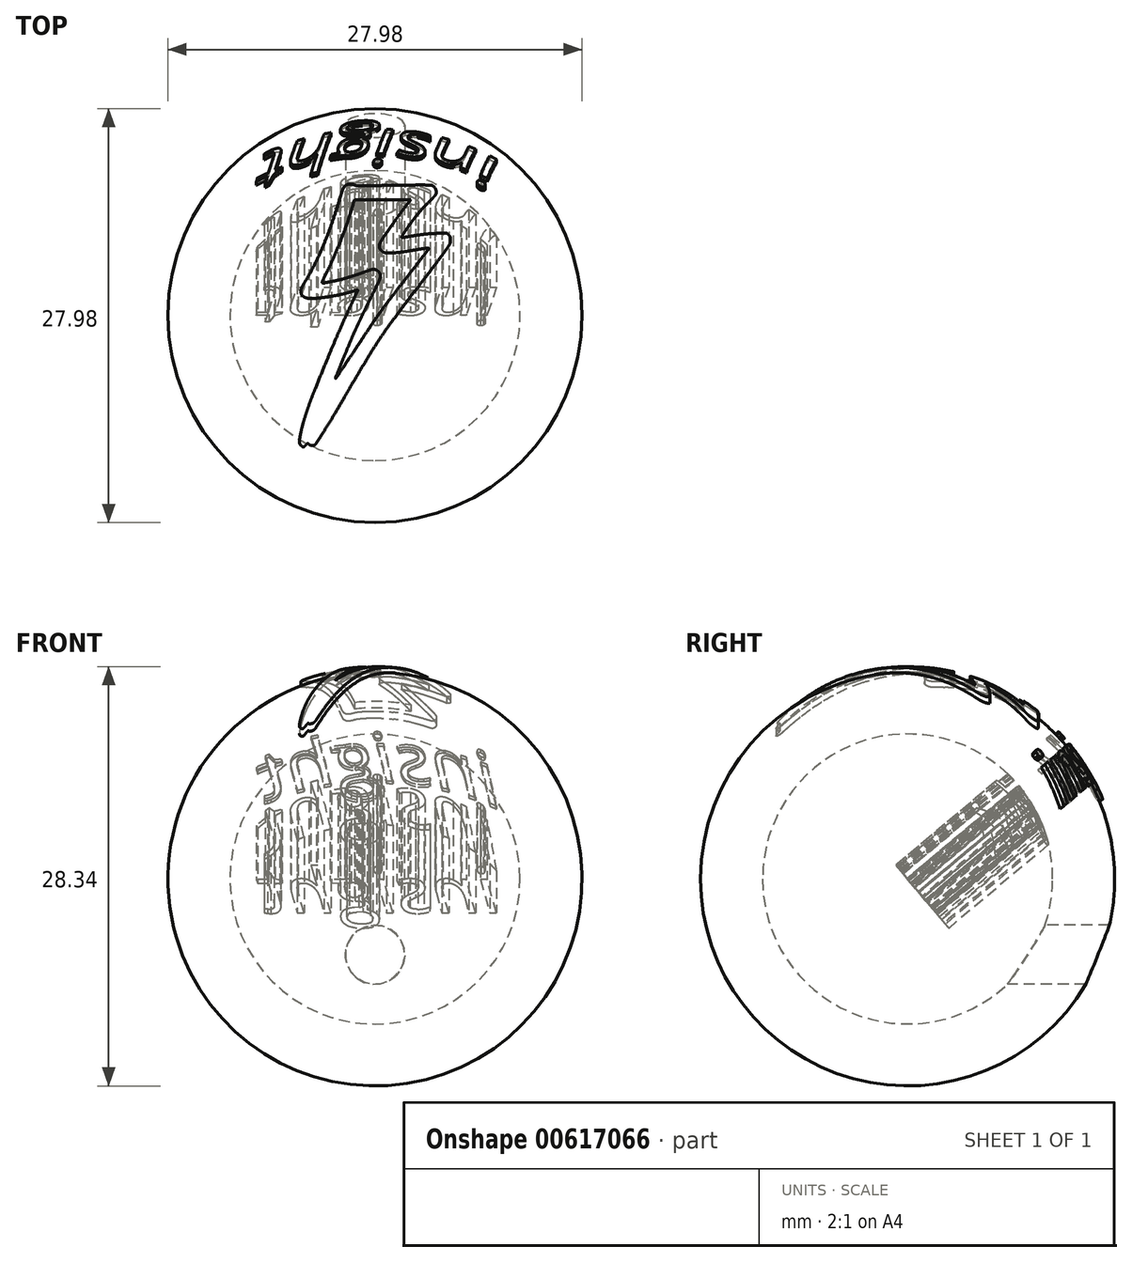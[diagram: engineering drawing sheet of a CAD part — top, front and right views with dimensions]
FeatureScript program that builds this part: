
annotation { "Feature Type Name" : "Feature", "Feature Type Description" : "" }
export const myFeature = defineFeature(function(context is Context, id is Id, definition is map)
    precondition{}
    {
        {
            var Q0;
            Q0=qCreatedBy(makeId("Top.planeOp"),FACE);
            var sketch = newSketch(context, id + "F0", { "sketchPlane" : qUnion([Q0])});
            skLineSegment(sketch, "E0", {"start": v(0, -10) * mm, "end": v(0, 10) * mm});
            skArc(sketch, "E1", {"start": v(0, 10) * mm, "mid": v(-10, 0) * mm, "end": v(0, -10) * mm});
            skSolve(sketch);
        }
        {
            var Q0;
            {var subQ0=sQuery(id+"F0.wireOp",EDGE,"E1");Q0=makeQuery(id+"F0.imprint","IMPRINT",FACE,{"disambiguationData":[TD([[makeQuery(id+"F0.imprint","IMPRINT",EDGE,{"derivedFrom":subQ0}),1.0]])]});}
            var Q1;
            Q1=sQuery(id+"F0.wireOp",EDGE,"E0");
            revolve(context, id + "F1", {"entities" : qUnion([Q0]), "axis" : qUnion([Q1]), "revolveType" : RevolveType.FULL});
        }
        {
            var Q0;
            Q0=makeQuery(id+"F1.opRevolve","SWEPT_BODY",BODY,{"disambiguationData":[OSD([sQuery(id+"F0.wireOp",EDGE,"E0"),sQuery(id+"F0.wireOp",EDGE,"E1")])]});
            var Q1;
            Q1=sQuery(id+"F0.wireOp",VERTEX,"NPe4G0ez-t7S9-9isL-QO5v-uuJu600mHcIT.center");
            var Q2;
            Q2=sQuery(id+"F0.wireOp",VERTEX,"E1.center");
            transform(context, id + "F2", {"entities" : qUnion([Q0]), "transformType" : TransformType.SCALE_UNIFORMLY, "scale" : 33.3, "scalePoint" : qUnion([Q2]), "makeCopy" : false});
        }
        {
            var Q0;
            Q0=qCreatedBy(makeId("Top.planeOp"),FACE);
            var sketch = newSketch(context, id + "F3", { "sketchPlane" : qUnion([Q0])});
            skArc(sketch, "E2", {"start": v(-47, 209.54) * mm, "mid": v(-48.28, 208.6) * mm, "end": v(-49.38, 207.48) * mm});
            skArc(sketch, "E3", {"start": v(-49.38, 207.48) * mm, "mid": v(-50.34, 206.13) * mm, "end": v(-51.1, 204.66) * mm});
            skArc(sketch, "E4", {"start": v(-51.1, 204.66) * mm, "mid": v(-52.12, 202.08) * mm, "end": v(-53.02, 199.45) * mm});
            skArc(sketch, "E5", {"start": v(-53.02, 199.45) * mm, "mid": v(-55.26, 192.2) * mm, "end": v(-57.48, 184.96) * mm});
            skArc(sketch, "E6", {"start": v(-57.48, 184.96) * mm, "mid": v(-63.5, 165.86) * mm, "end": v(-69.92, 146.9) * mm});
            skArc(sketch, "E7", {"start": v(-69.92, 146.9) * mm, "mid": v(-76.05, 130.2) * mm, "end": v(-82.66, 113.68) * mm});
            skArc(sketch, "E8", {"start": v(-82.66, 113.68) * mm, "mid": v(-89.16, 98.83) * mm, "end": v(-96.13, 84.2) * mm});
            skArc(sketch, "E9", {"start": v(-96.13, 84.2) * mm, "mid": v(-103.18, 70.68) * mm, "end": v(-110.76, 57.45) * mm});
            skArc(sketch, "E10", {"start": v(-110.76, 57.45) * mm, "mid": v(-113.7, 52.45) * mm, "end": v(-116.55, 47.39) * mm});
            skArc(sketch, "E11", {"start": v(-116.55, 47.39) * mm, "mid": v(-117.87, 44.67) * mm, "end": v(-118.89, 41.82) * mm});
            skArc(sketch, "E12", {"start": v(-118.89, 41.82) * mm, "mid": v(-119.28, 39.76) * mm, "end": v(-119.24, 37.66) * mm});
            skArc(sketch, "E13", {"start": v(-119.24, 37.66) * mm, "mid": v(-118.78, 35.5) * mm, "end": v(-117.95, 33.47) * mm});
            skArc(sketch, "E14", {"start": v(-117.95, 33.47) * mm, "mid": v(-117.53, 32.77) * mm, "end": v(-117.02, 32.12) * mm});
            skArc(sketch, "E15", {"start": v(-117.02, 32.12) * mm, "mid": v(-116.39, 31.48) * mm, "end": v(-115.7, 30.9) * mm});
            skArc(sketch, "E16", {"start": v(-115.7, 30.9) * mm, "mid": v(-114.87, 30.32) * mm, "end": v(-114, 29.8) * mm});
            skArc(sketch, "E17", {"start": v(-114, 29.8) * mm, "mid": v(-113, 29.32) * mm, "end": v(-111.97, 28.89) * mm});
            skArc(sketch, "E18", {"start": v(-111.97, 28.89) * mm, "mid": v(-106.69, 27.5) * mm, "end": v(-101.23, 27.25) * mm});
            skArc(sketch, "E19", {"start": v(-101.23, 27.25) * mm, "mid": v(-90.7, 28.1) * mm, "end": v(-80.2, 29.33) * mm});
            skArc(sketch, "E20", {"start": v(-80.2, 29.33) * mm, "mid": v(-68.36, 31.17) * mm, "end": v(-56.6, 33.47) * mm});
            skArc(sketch, "E21", {"start": v(-56.6, 33.47) * mm, "mid": v(-45.47, 36.14) * mm, "end": v(-34.47, 39.32) * mm});
            skArc(sketch, "E22", {"start": v(-34.47, 39.32) * mm, "mid": v(-33.22, 39.7) * mm, "end": v(-31.97, 40.07) * mm});
            skArc(sketch, "E23", {"start": v(-31.97, 40.07) * mm, "mid": v(-30.9, 40.37) * mm, "end": v(-29.82, 40.66) * mm});
            skArc(sketch, "E24", {"start": v(-29.82, 40.66) * mm, "mid": v(-28.9, 40.88) * mm, "end": v(-27.98, 41.1) * mm});
            skArc(sketch, "E25", {"start": v(-27.98, 41.1) * mm, "mid": v(-27.83, 41.1) * mm, "end": v(-27.7, 41.03) * mm});
            skArc(sketch, "E26", {"start": v(-27.7, 41.03) * mm, "mid": v(-27.63, 40.9) * mm, "end": v(-27.65, 40.74) * mm});
            skArc(sketch, "E27", {"start": v(-27.65, 40.74) * mm, "mid": v(-29.01, 37.7) * mm, "end": v(-30.38, 34.67) * mm});
            skArc(sketch, "E28", {"start": v(-30.38, 34.67) * mm, "mid": v(-31.94, 31.26) * mm, "end": v(-33.51, 27.85) * mm});
            skArc(sketch, "E29", {"start": v(-33.51, 27.85) * mm, "mid": v(-35.4, 23.83) * mm, "end": v(-37.29, 19.82) * mm});
            skArc(sketch, "E30", {"start": v(-37.29, 19.82) * mm, "mid": v(-43.49, 6.55) * mm, "end": v(-49.54, -6.8) * mm});
            skArc(sketch, "E31", {"start": v(-49.54, -6.8) * mm, "mid": v(-56.04, -21.49) * mm, "end": v(-62.42, -36.24) * mm});
            skArc(sketch, "E32", {"start": v(-62.42, -36.24) * mm, "mid": v(-70.03, -54.2) * mm, "end": v(-77.53, -72.22) * mm});
            skArc(sketch, "E33", {"start": v(-77.53, -72.22) * mm, "mid": v(-87.24, -95.89) * mm, "end": v(-96.88, -119.58) * mm});
            skArc(sketch, "E34", {"start": v(-96.88, -119.58) * mm, "mid": v(-100.55, -128.83) * mm, "end": v(-104.07, -138.15) * mm});
            skArc(sketch, "E35", {"start": v(-104.07, -138.15) * mm, "mid": v(-107.3, -147.19) * mm, "end": v(-110.39, -156.28) * mm});
            skArc(sketch, "E36", {"start": v(-110.39, -156.28) * mm, "mid": v(-113, -164.53) * mm, "end": v(-115.47, -172.82) * mm});
            skArc(sketch, "E37", {"start": v(-115.47, -172.82) * mm, "mid": v(-117.29, -179.6) * mm, "end": v(-118.86, -186.44) * mm});
            skArc(sketch, "E38", {"start": v(-118.86, -186.44) * mm, "mid": v(-119.99, -191.95) * mm, "end": v(-121.04, -197.48) * mm});
            skArc(sketch, "E39", {"start": v(-121.04, -197.48) * mm, "mid": v(-121.43, -200.27) * mm, "end": v(-121.57, -203.08) * mm});
            skArc(sketch, "E40", {"start": v(-121.57, -203.08) * mm, "mid": v(-121.42, -204.86) * mm, "end": v(-120.93, -206.57) * mm});
            skArc(sketch, "E41", {"start": v(-120.93, -206.57) * mm, "mid": v(-120.15, -208.02) * mm, "end": v(-119.04, -209.23) * mm});
            skArc(sketch, "E42", {"start": v(-119.04, -209.23) * mm, "mid": v(-117.89, -210.16) * mm, "end": v(-116.67, -211) * mm});
            skArc(sketch, "E43", {"start": v(-116.67, -211) * mm, "mid": v(-115.93, -211.32) * mm, "end": v(-115.12, -211.37) * mm});
            skArc(sketch, "E44", {"start": v(-115.12, -211.37) * mm, "mid": v(-114.28, -211.14) * mm, "end": v(-113.53, -210.67) * mm});
            skArc(sketch, "E45", {"start": v(-113.53, -210.67) * mm, "mid": v(-112.18, -209.48) * mm, "end": v(-110.88, -208.23) * mm});
            skArc(sketch, "E46", {"start": v(-110.88, -208.23) * mm, "mid": v(-110.09, -207.46) * mm, "end": v(-109.28, -206.72) * mm});
            skArc(sketch, "E47", {"start": v(-109.28, -206.72) * mm, "mid": v(-108.75, -206.3) * mm, "end": v(-108.19, -205.97) * mm});
            skArc(sketch, "E48", {"start": v(-108.19, -205.97) * mm, "mid": v(-107.84, -205.86) * mm, "end": v(-107.47, -205.86) * mm});
            skArc(sketch, "E49", {"start": v(-107.47, -205.86) * mm, "mid": v(-107.19, -205.98) * mm, "end": v(-107, -206.23) * mm});
            skArc(sketch, "E50", {"start": v(-107, -206.23) * mm, "mid": v(-106.57, -207.01) * mm, "end": v(-105.92, -207.63) * mm});
            skArc(sketch, "E51", {"start": v(-105.92, -207.63) * mm, "mid": v(-104.9, -208.26) * mm, "end": v(-103.81, -208.75) * mm});
            skArc(sketch, "E52", {"start": v(-103.81, -208.75) * mm, "mid": v(-102.6, -209.13) * mm, "end": v(-101.34, -209.36) * mm});
            skArc(sketch, "E53", {"start": v(-101.34, -209.36) * mm, "mid": v(-100.23, -209.39) * mm, "end": v(-99.13, -209.22) * mm});
            skArc(sketch, "E54", {"start": v(-99.13, -209.22) * mm, "mid": v(-96.8, -208.14) * mm, "end": v(-95, -206.3) * mm});
            skArc(sketch, "E55", {"start": v(-95, -206.3) * mm, "mid": v(-88.97, -197.13) * mm, "end": v(-83.04, -187.9) * mm});
            skArc(sketch, "E56", {"start": v(-83.04, -187.9) * mm, "mid": v(-74.78, -174.65) * mm, "end": v(-66.71, -161.28) * mm});
            skArc(sketch, "E57", {"start": v(-66.71, -161.28) * mm, "mid": v(-54.28, -140.2) * mm, "end": v(-41.93, -119.08) * mm});
            skArc(sketch, "E58", {"start": v(-41.93, -119.08) * mm, "mid": v(-27, -93.64) * mm, "end": v(-11.87, -68.32) * mm});
            skArc(sketch, "E59", {"start": v(-11.87, -68.32) * mm, "mid": v(-1.4, -51.44) * mm, "end": v(9.47, -34.82) * mm});
            skArc(sketch, "E60", {"start": v(9.47, -34.82) * mm, "mid": v(20.75, -18.5) * mm, "end": v(32.43, -2.45) * mm});
            skArc(sketch, "E61", {"start": v(32.43, -2.45) * mm, "mid": v(50.15, 21.06) * mm, "end": v(68.05, 44.42) * mm});
            skArc(sketch, "E62", {"start": v(68.05, 44.42) * mm, "mid": v(76.36, 55.22) * mm, "end": v(84.65, 66.03) * mm});
            skArc(sketch, "E63", {"start": v(84.65, 66.03) * mm, "mid": v(91.6, 75.18) * mm, "end": v(98.52, 84.35) * mm});
            skArc(sketch, "E64", {"start": v(98.52, 84.35) * mm, "mid": v(104, 91.7) * mm, "end": v(109.45, 99.07) * mm});
            skArc(sketch, "E65", {"start": v(109.45, 99.07) * mm, "mid": v(112.83, 103.75) * mm, "end": v(116.12, 108.5) * mm});
            skArc(sketch, "E66", {"start": v(116.12, 108.5) * mm, "mid": v(117.67, 110.82) * mm, "end": v(119.18, 113.17) * mm});
            skArc(sketch, "E67", {"start": v(119.18, 113.17) * mm, "mid": v(119.98, 114.55) * mm, "end": v(120.65, 116) * mm});
            skArc(sketch, "E68", {"start": v(120.65, 116) * mm, "mid": v(121.08, 117.22) * mm, "end": v(121.35, 118.48) * mm});
            skArc(sketch, "E69", {"start": v(121.35, 118.48) * mm, "mid": v(121.51, 120) * mm, "end": v(121.57, 121.54) * mm});
            skArc(sketch, "E70", {"start": v(121.57, 121.54) * mm, "mid": v(121.54, 122.95) * mm, "end": v(121.45, 124.35) * mm});
            skArc(sketch, "E71", {"start": v(121.45, 124.35) * mm, "mid": v(121.3, 125.3) * mm, "end": v(121.02, 126.22) * mm});
            skArc(sketch, "E72", {"start": v(121.02, 126.22) * mm, "mid": v(120.64, 127.04) * mm, "end": v(120.14, 127.8) * mm});
            skArc(sketch, "E73", {"start": v(120.14, 127.8) * mm, "mid": v(119.36, 128.74) * mm, "end": v(118.52, 129.63) * mm});
            skLineSegment(sketch, "E74", {"start": v(118.52, 129.63) * mm, "end": v(115.47, 132.68) * mm});
            skLineSegment(sketch, "E75", {"start": v(115.47, 132.68) * mm, "end": v(98.77, 132.14) * mm});
            skArc(sketch, "E76", {"start": v(98.77, 132.14) * mm, "mid": v(94.4, 131.97) * mm, "end": v(90.03, 131.72) * mm});
            skArc(sketch, "E77", {"start": v(90.03, 131.72) * mm, "mid": v(85.84, 131.4) * mm, "end": v(81.65, 131.01) * mm});
            skArc(sketch, "E78", {"start": v(81.65, 131.01) * mm, "mid": v(77.34, 130.53) * mm, "end": v(73.04, 129.97) * mm});
            skArc(sketch, "E79", {"start": v(73.04, 129.97) * mm, "mid": v(68.3, 129.28) * mm, "end": v(63.57, 128.52) * mm});
            skArc(sketch, "E80", {"start": v(63.57, 128.52) * mm, "mid": v(59.96, 127.92) * mm, "end": v(56.35, 127.34) * mm});
            skArc(sketch, "E81", {"start": v(56.35, 127.34) * mm, "mid": v(53.16, 126.83) * mm, "end": v(49.97, 126.34) * mm});
            skArc(sketch, "E82", {"start": v(49.97, 126.34) * mm, "mid": v(47.26, 125.93) * mm, "end": v(44.55, 125.53) * mm});
            skArc(sketch, "E83", {"start": v(44.55, 125.53) * mm, "mid": v(43.9, 125.45) * mm, "end": v(43.25, 125.43) * mm});
            skArc(sketch, "E84", {"start": v(43.25, 125.43) * mm, "mid": v(42.86, 125.61) * mm, "end": v(42.77, 126.03) * mm});
            skArc(sketch, "E85", {"start": v(42.77, 126.03) * mm, "mid": v(43.04, 126.93) * mm, "end": v(43.43, 127.78) * mm});
            skArc(sketch, "E86", {"start": v(43.43, 127.78) * mm, "mid": v(44.33, 129.4) * mm, "end": v(45.32, 130.97) * mm});
            skArc(sketch, "E87", {"start": v(45.32, 130.97) * mm, "mid": v(47.23, 133.83) * mm, "end": v(49.18, 136.67) * mm});
            skArc(sketch, "E88", {"start": v(49.18, 136.67) * mm, "mid": v(54.18, 143.84) * mm, "end": v(59.27, 150.95) * mm});
            skArc(sketch, "E89", {"start": v(59.27, 150.95) * mm, "mid": v(63.33, 156.4) * mm, "end": v(67.53, 161.75) * mm});
            skArc(sketch, "E90", {"start": v(67.53, 161.75) * mm, "mid": v(71.4, 166.4) * mm, "end": v(75.39, 170.92) * mm});
            skArc(sketch, "E91", {"start": v(75.39, 170.92) * mm, "mid": v(79.69, 175.52) * mm, "end": v(84.11, 180.02) * mm});
            skArc(sketch, "E92", {"start": v(84.11, 180.02) * mm, "mid": v(86.5, 182.4) * mm, "end": v(88.88, 184.8) * mm});
            skArc(sketch, "E93", {"start": v(88.88, 184.8) * mm, "mid": v(90.99, 186.98) * mm, "end": v(93.07, 189.17) * mm});
            skArc(sketch, "E94", {"start": v(93.07, 189.17) * mm, "mid": v(94.8, 191.03) * mm, "end": v(96.53, 192.9) * mm});
            skArc(sketch, "E95", {"start": v(96.53, 192.9) * mm, "mid": v(97.03, 193.52) * mm, "end": v(97.45, 194.2) * mm});
            skArc(sketch, "E96", {"start": v(97.45, 194.2) * mm, "mid": v(98.2, 196.08) * mm, "end": v(98.5, 198.08) * mm});
            skArc(sketch, "E97", {"start": v(98.5, 198.08) * mm, "mid": v(98.4, 200.27) * mm, "end": v(97.9, 202.4) * mm});
            skArc(sketch, "E98", {"start": v(97.9, 202.4) * mm, "mid": v(97.03, 204.43) * mm, "end": v(95.8, 206.27) * mm});
            skArc(sketch, "E99", {"start": v(95.8, 206.27) * mm, "mid": v(94.34, 207.76) * mm, "end": v(92.6, 208.9) * mm});
            skArc(sketch, "E100", {"start": v(92.6, 208.9) * mm, "mid": v(91.01, 209.52) * mm, "end": v(89.33, 209.78) * mm});
            skArc(sketch, "E101", {"start": v(89.33, 209.78) * mm, "mid": v(84.65, 209.93) * mm, "end": v(79.96, 210.01) * mm});
            skArc(sketch, "E102", {"start": v(79.96, 210.01) * mm, "mid": v(72.03, 210.05) * mm, "end": v(64.1, 209.99) * mm});
            skArc(sketch, "E103", {"start": v(64.1, 209.99) * mm, "mid": v(46.76, 209.76) * mm, "end": v(29.42, 209.5) * mm});
            skArc(sketch, "E104", {"start": v(29.42, 209.5) * mm, "mid": v(12.64, 209.26) * mm, "end": v(-4.14, 209.04) * mm});
            skArc(sketch, "E105", {"start": v(-4.14, 209.04) * mm, "mid": v(-12.26, 208.98) * mm, "end": v(-20.37, 209) * mm});
            skArc(sketch, "E106", {"start": v(-20.37, 209) * mm, "mid": v(-25.38, 209.07) * mm, "end": v(-30.39, 209.19) * mm});
            skArc(sketch, "E107", {"start": v(-30.39, 209.19) * mm, "mid": v(-31.67, 209.42) * mm, "end": v(-32.84, 210) * mm});
            skArc(sketch, "E108", {"start": v(-32.84, 210) * mm, "mid": v(-34.16, 210.72) * mm, "end": v(-35.6, 211.12) * mm});
            skArc(sketch, "E109", {"start": v(-35.6, 211.12) * mm, "mid": v(-37.61, 211.34) * mm, "end": v(-39.63, 211.37) * mm});
            skArc(sketch, "E110", {"start": v(-39.63, 211.37) * mm, "mid": v(-41.72, 211.2) * mm, "end": v(-43.79, 210.84) * mm});
            skArc(sketch, "E111", {"start": v(-43.79, 210.84) * mm, "mid": v(-45.45, 210.32) * mm, "end": v(-47, 209.54) * mm});
            skArc(sketch, "E112", {"start": v(55.04, 183.12) * mm, "mid": v(51.95, 179.25) * mm, "end": v(48.92, 175.34) * mm});
            skArc(sketch, "E113", {"start": v(48.92, 175.34) * mm, "mid": v(45.58, 170.93) * mm, "end": v(42.28, 166.49) * mm});
            skArc(sketch, "E114", {"start": v(42.28, 166.49) * mm, "mid": v(38.29, 161) * mm, "end": v(34.33, 155.49) * mm});
            skArc(sketch, "E115", {"start": v(34.33, 155.49) * mm, "mid": v(29.19, 148.22) * mm, "end": v(24.07, 140.94) * mm});
            skArc(sketch, "E116", {"start": v(24.07, 140.94) * mm, "mid": v(17.9, 132.06) * mm, "end": v(11.83, 123.12) * mm});
            skArc(sketch, "E117", {"start": v(11.83, 123.12) * mm, "mid": v(9.53, 119.34) * mm, "end": v(7.6, 115.36) * mm});
            skArc(sketch, "E118", {"start": v(7.6, 115.36) * mm, "mid": v(6.92, 112.88) * mm, "end": v(6.94, 110.3) * mm});
            skArc(sketch, "E119", {"start": v(6.94, 110.3) * mm, "mid": v(7.64, 107.86) * mm, "end": v(9, 105.7) * mm});
            skArc(sketch, "E120", {"start": v(9, 105.7) * mm, "mid": v(9.6, 105.02) * mm, "end": v(10.27, 104.4) * mm});
            skArc(sketch, "E121", {"start": v(10.27, 104.4) * mm, "mid": v(11.09, 103.74) * mm, "end": v(11.94, 103.12) * mm});
            skArc(sketch, "E122", {"start": v(11.94, 103.12) * mm, "mid": v(12.8, 102.56) * mm, "end": v(13.7, 102.04) * mm});
            skArc(sketch, "E123", {"start": v(13.7, 102.04) * mm, "mid": v(14.49, 101.66) * mm, "end": v(15.3, 101.35) * mm});
            skArc(sketch, "E124", {"start": v(15.3, 101.35) * mm, "mid": v(18.1, 100.67) * mm, "end": v(20.97, 100.47) * mm});
            skArc(sketch, "E125", {"start": v(20.97, 100.47) * mm, "mid": v(26.03, 100.6) * mm, "end": v(31.08, 100.9) * mm});
            skArc(sketch, "E126", {"start": v(31.08, 100.9) * mm, "mid": v(37.67, 101.52) * mm, "end": v(44.24, 102.34) * mm});
            skArc(sketch, "E127", {"start": v(44.24, 102.34) * mm, "mid": v(52.42, 103.55) * mm, "end": v(60.57, 104.88) * mm});
            skArc(sketch, "E128", {"start": v(60.57, 104.88) * mm, "mid": v(67.14, 106) * mm, "end": v(73.7, 107.07) * mm});
            skArc(sketch, "E129", {"start": v(73.7, 107.07) * mm, "mid": v(77.4, 107.63) * mm, "end": v(81.12, 108.1) * mm});
            skArc(sketch, "E130", {"start": v(81.12, 108.1) * mm, "mid": v(83.48, 108.33) * mm, "end": v(85.85, 108.52) * mm});
            skArc(sketch, "E131", {"start": v(85.85, 108.52) * mm, "mid": v(86.36, 108.33) * mm, "end": v(86.57, 107.84) * mm});
            skArc(sketch, "E132", {"start": v(86.57, 107.84) * mm, "mid": v(86.49, 107.34) * mm, "end": v(86.25, 106.9) * mm});
            skArc(sketch, "E133", {"start": v(86.25, 106.9) * mm, "mid": v(81.5, 100.69) * mm, "end": v(76.75, 94.48) * mm});
            skArc(sketch, "E134", {"start": v(76.75, 94.48) * mm, "mid": v(70.88, 86.84) * mm, "end": v(64.97, 79.23) * mm});
            skArc(sketch, "E135", {"start": v(64.97, 79.23) * mm, "mid": v(56.84, 68.82) * mm, "end": v(48.7, 58.42) * mm});
            skArc(sketch, "E136", {"start": v(48.7, 58.42) * mm, "mid": v(39.42, 46.53) * mm, "end": v(30.2, 34.58) * mm});
            skArc(sketch, "E137", {"start": v(30.2, 34.58) * mm, "mid": v(22.75, 24.8) * mm, "end": v(15.4, 14.95) * mm});
            skArc(sketch, "E138", {"start": v(15.4, 14.95) * mm, "mid": v(9.27, 6.56) * mm, "end": v(3.24, -1.9) * mm});
            skArc(sketch, "E139", {"start": v(3.24, -1.9) * mm, "mid": v(-2, -9.44) * mm, "end": v(-7.1, -17.08) * mm});
            skArc(sketch, "E140", {"start": v(-7.1, -17.08) * mm, "mid": v(-18.13, -33.82) * mm, "end": v(-29.19, -50.55) * mm});
            skArc(sketch, "E141", {"start": v(-29.19, -50.55) * mm, "mid": v(-38.12, -64.02) * mm, "end": v(-47.09, -77.46) * mm});
            skArc(sketch, "E142", {"start": v(-47.09, -77.46) * mm, "mid": v(-54.97, -89.25) * mm, "end": v(-62.85, -101.03) * mm});
            skArc(sketch, "E143", {"start": v(-62.85, -101.03) * mm, "mid": v(-63.05, -101.15) * mm, "end": v(-63.26, -101.07) * mm});
            skArc(sketch, "E144", {"start": v(-63.26, -101.07) * mm, "mid": v(-63.52, -100.6) * mm, "end": v(-63.47, -100.08) * mm});
            skArc(sketch, "E145", {"start": v(-63.47, -100.08) * mm, "mid": v(-57.76, -85.98) * mm, "end": v(-52.06, -71.89) * mm});
            skArc(sketch, "E146", {"start": v(-52.06, -71.89) * mm, "mid": v(-46.78, -58.95) * mm, "end": v(-41.44, -46.04) * mm});
            skArc(sketch, "E147", {"start": v(-41.44, -46.04) * mm, "mid": v(-37.33, -36.33) * mm, "end": v(-33.11, -26.67) * mm});
            skArc(sketch, "E148", {"start": v(-33.11, -26.67) * mm, "mid": v(-30.81, -21.55) * mm, "end": v(-28.46, -16.44) * mm});
            skArc(sketch, "E149", {"start": v(-28.46, -16.44) * mm, "mid": v(-25.1, -9.3) * mm, "end": v(-21.72, -2.17) * mm});
            skArc(sketch, "E150", {"start": v(-21.72, -2.17) * mm, "mid": v(-18, 5.59) * mm, "end": v(-14.25, 13.33) * mm});
            skArc(sketch, "E151", {"start": v(-14.25, 13.33) * mm, "mid": v(-10.7, 20.58) * mm, "end": v(-7.13, 27.81) * mm});
            skArc(sketch, "E152", {"start": v(-7.13, 27.81) * mm, "mid": v(-0.89, 40.43) * mm, "end": v(5.29, 53.08) * mm});
            skArc(sketch, "E153", {"start": v(5.29, 53.08) * mm, "mid": v(7.1, 57.26) * mm, "end": v(8.5, 61.59) * mm});
            skArc(sketch, "E154", {"start": v(8.5, 61.59) * mm, "mid": v(8.8, 64.16) * mm, "end": v(8.26, 66.7) * mm});
            skArc(sketch, "E155", {"start": v(8.26, 66.7) * mm, "mid": v(6.91, 69.22) * mm, "end": v(5, 71.35) * mm});
            skArc(sketch, "E156", {"start": v(5, 71.35) * mm, "mid": v(3.35, 72.6) * mm, "end": v(1.52, 73.58) * mm});
            skArc(sketch, "E157", {"start": v(1.52, 73.58) * mm, "mid": v(-0.24, 74.14) * mm, "end": v(-2.07, 74.3) * mm});
            skArc(sketch, "E158", {"start": v(-2.07, 74.3) * mm, "mid": v(-4.42, 74.1) * mm, "end": v(-6.73, 73.58) * mm});
            skArc(sketch, "E159", {"start": v(-6.73, 73.58) * mm, "mid": v(-10.43, 72.38) * mm, "end": v(-14.1, 71.06) * mm});
            skArc(sketch, "E160", {"start": v(-14.1, 71.06) * mm, "mid": v(-19.11, 69.2) * mm, "end": v(-24.16, 67.41) * mm});
            skArc(sketch, "E161", {"start": v(-24.16, 67.41) * mm, "mid": v(-30.1, 65.41) * mm, "end": v(-36.05, 63.48) * mm});
            skArc(sketch, "E162", {"start": v(-36.05, 63.48) * mm, "mid": v(-41.81, 61.67) * mm, "end": v(-47.6, 59.93) * mm});
            skArc(sketch, "E163", {"start": v(-47.6, 59.93) * mm, "mid": v(-52, 58.68) * mm, "end": v(-56.43, 57.55) * mm});
            skArc(sketch, "E164", {"start": v(-56.43, 57.55) * mm, "mid": v(-60.13, 56.68) * mm, "end": v(-63.84, 55.88) * mm});
            skArc(sketch, "E165", {"start": v(-63.84, 55.88) * mm, "mid": v(-68.26, 55) * mm, "end": v(-72.68, 54.16) * mm});
            skArc(sketch, "E166", {"start": v(-72.68, 54.16) * mm, "mid": v(-76.85, 53.42) * mm, "end": v(-81.02, 52.7) * mm});
            skArc(sketch, "E167", {"start": v(-81.02, 52.7) * mm, "mid": v(-82.74, 52.5) * mm, "end": v(-84.47, 52.42) * mm});
            skArc(sketch, "E168", {"start": v(-84.47, 52.42) * mm, "mid": v(-84.94, 52.66) * mm, "end": v(-85.04, 53.17) * mm});
            skArc(sketch, "E169", {"start": v(-85.04, 53.17) * mm, "mid": v(-84.56, 54.71) * mm, "end": v(-83.99, 56.23) * mm});
            skArc(sketch, "E170", {"start": v(-83.99, 56.23) * mm, "mid": v(-82.83, 58.9) * mm, "end": v(-81.6, 61.54) * mm});
            skArc(sketch, "E171", {"start": v(-81.6, 61.54) * mm, "mid": v(-79.09, 66.62) * mm, "end": v(-76.56, 71.67) * mm});
            skArc(sketch, "E172", {"start": v(-76.56, 71.67) * mm, "mid": v(-70.88, 83.38) * mm, "end": v(-65.59, 95.27) * mm});
            skArc(sketch, "E173", {"start": v(-65.59, 95.27) * mm, "mid": v(-59.57, 109.73) * mm, "end": v(-53.83, 124.3) * mm});
            skArc(sketch, "E174", {"start": v(-53.83, 124.3) * mm, "mid": v(-48.29, 139.13) * mm, "end": v(-43.02, 154.06) * mm});
            skArc(sketch, "E175", {"start": v(-43.02, 154.06) * mm, "mid": v(-38.8, 166.98) * mm, "end": v(-34.95, 180.02) * mm});
            skLineSegment(sketch, "E176", {"start": v(-34.95, 180.02) * mm, "end": v(-33.25, 186.12) * mm});
            skLineSegment(sketch, "E177", {"start": v(-33.25, 186.12) * mm, "end": v(12.19, 186.21) * mm});
            skLineSegment(sketch, "E178", {"start": v(12.19, 186.21) * mm, "end": v(57.63, 186.3) * mm});
            skLineSegment(sketch, "E179", {"start": v(57.63, 186.3) * mm, "end": v(55.04, 183.12) * mm});
            skSolve(sketch);
        }
        {
            var Q0;
            Q0=qSketchRegion(id+"F3",true);
            var Q1;
            Q1=sQuery(id+"F3.wireOp",EDGE,"c928f899-12af-4b01-b412-b3b7da3d830f");
            var Q2;
            Q2=sQuery(id+"F3.wireOp",EDGE,"b69f99c7-a6d0-4d1b-8752-9e82ab4c99ec");
            extrude(context, id + "F4", {"entities" : qUnion([Q0]), "operationType" : NewBodyOperationType.ADD, "surfaceEntities" : qUnion([Q1, Q2]), "depth" : 350 * mm});
        }
        {
            var Q0;
            Q0=makeQuery(id+"F4.opExtrude","SWEPT_BODY",BODY,{"disambiguationData":[OSD([sQuery(id+"F3.wireOp",EDGE,"15c6da4e-992d-4824-9d20-70d2d6be9970"),sQuery(id+"F3.wireOp",EDGE,"268c69ec-46be-456f-85eb-69decc32fe39"),sQuery(id+"F3.wireOp",EDGE,"1d386307-6059-4203-bca6-0c1cec3c82e1"),sQuery(id+"F3.wireOp",EDGE,"7d7c66d2-f869-427f-806b-ad436cacd60e"),sQuery(id+"F3.wireOp",EDGE,"1db91850-860e-493f-a3af-7a0f3f1512ae"),sQuery(id+"F3.wireOp",EDGE,"2c65f23b-9f03-4f6f-ab37-de452af29e3c"),sQuery(id+"F3.wireOp",EDGE,"ba006cbc-bbd7-44d9-84cc-9cde0967c280"),sQuery(id+"F3.wireOp",EDGE,"ae950208-c781-4a25-8fcf-ffe59b9085ff"),sQuery(id+"F3.wireOp",EDGE,"3cce0944-c62d-4831-9b9d-d1a418d328b4"),sQuery(id+"F3.wireOp",EDGE,"9edc5e7d-16c0-40c4-98ad-6b91d5df0e78"),sQuery(id+"F3.wireOp",EDGE,"aa452f44-44a2-4c64-bff5-a2a639df00db"),sQuery(id+"F3.wireOp",EDGE,"16259f99-ce20-4b7b-81e1-fa0909c03eb4"),sQuery(id+"F3.wireOp",EDGE,"79895566-a943-429d-b257-d76af3645bdf"),sQuery(id+"F3.wireOp",EDGE,"a85490ef-f17e-45c8-b92b-28215162778a"),sQuery(id+"F3.wireOp",EDGE,"322f1036-a6fd-4992-ab69-5919540af7a6"),sQuery(id+"F3.wireOp",EDGE,"0a87ff38-4ab4-4140-b3c3-2d7501d9f3b1"),sQuery(id+"F3.wireOp",EDGE,"a6e7bdf2-ef3e-49d4-9b3c-e34f5a41e0c4"),sQuery(id+"F3.wireOp",EDGE,"3e588790-576f-47c1-9730-f5e27fa1e8f9"),sQuery(id+"F3.wireOp",EDGE,"ce3739ef-15fd-4754-ad9c-ccf511a9a8fb"),sQuery(id+"F3.wireOp",EDGE,"201134a3-66f3-4a3f-aa9b-76948966efc0"),sQuery(id+"F3.wireOp",EDGE,"65b511ea-0759-428d-8070-88e1f521d8ea"),sQuery(id+"F3.wireOp",EDGE,"c37cddb6-5cf8-4891-aff4-7191a72080b9"),sQuery(id+"F3.wireOp",EDGE,"52a43dbd-e952-43e1-be3d-d70e107260e6"),sQuery(id+"F3.wireOp",EDGE,"08c1271f-f5c3-4f26-be27-7f5e21217dff"),sQuery(id+"F3.wireOp",EDGE,"59a09f58-0503-4180-962a-e04db21f0da8"),sQuery(id+"F3.wireOp",EDGE,"e56a4626-e956-42c3-bb5d-cd9dae1ca801"),sQuery(id+"F3.wireOp",EDGE,"5ff5d55f-af90-49eb-8040-353101557de8"),sQuery(id+"F3.wireOp",EDGE,"0ed7430b-e164-4f56-8af9-4534524aa7c0"),sQuery(id+"F3.wireOp",EDGE,"b5610a6e-b6bb-43e3-9a8d-d3d7c5f0098b"),sQuery(id+"F3.wireOp",EDGE,"1d417af8-88ad-47c2-a4e2-6fec82bd6695"),sQuery(id+"F3.wireOp",EDGE,"778ae99a-956a-4ddb-8078-d9bc57f9fc8e"),sQuery(id+"F3.wireOp",EDGE,"5b19af09-f144-446e-9dfa-8766819c9efd"),sQuery(id+"F3.wireOp",EDGE,"028339f6-0475-4a57-af8d-550e32ad7466"),sQuery(id+"F3.wireOp",EDGE,"d5ae35b6-d210-433a-92c8-e92622696872"),sQuery(id+"F3.wireOp",EDGE,"16a2e606-2caa-4876-9ffa-8f08c4ff3a37"),sQuery(id+"F3.wireOp",EDGE,"5b90b144-be56-4de7-a9dd-c1e0336acbe3"),sQuery(id+"F3.wireOp",EDGE,"5912d126-c5fc-41e4-bfb8-b4fefc52ca72"),sQuery(id+"F3.wireOp",EDGE,"2e96ce95-bd3e-4f27-a7f8-b62cf5efe954"),sQuery(id+"F3.wireOp",EDGE,"ecb4e259-1207-4dd0-bc3c-87c6506cc3a5"),sQuery(id+"F3.wireOp",EDGE,"105fb72e-4d79-4204-af2f-b3b26f5eb8d1"),sQuery(id+"F3.wireOp",EDGE,"fa59b598-df54-48c6-bb8f-c5f7618c69d0"),sQuery(id+"F3.wireOp",EDGE,"a6beef0d-f124-47ac-b957-e6cd3057a354"),sQuery(id+"F3.wireOp",EDGE,"7c3eaf53-dcb7-43b1-ad18-80ff953eb59e"),sQuery(id+"F3.wireOp",EDGE,"281fe206-104f-408f-94b6-be79f12604c9")])]});
            var Q1;
            Q1=makeQuery(id+"F4.opExtrude","SWEPT_BODY",BODY,{"disambiguationData":[OSD([sQuery(id+"F3.wireOp",EDGE,"58f6206a-5554-41d4-8cf7-6e0b4724a469"),sQuery(id+"F3.wireOp",EDGE,"85dabe77-b6aa-43d5-a519-64383616f71e"),sQuery(id+"F3.wireOp",EDGE,"4b679fe6-9e11-497d-b8fd-14ca14e49ddd"),sQuery(id+"F3.wireOp",EDGE,"51de25f6-d59e-4805-a327-1fd7e38869c8"),sQuery(id+"F3.wireOp",EDGE,"d47977fb-70d3-4df8-bc35-66fcc0e556e0"),sQuery(id+"F3.wireOp",EDGE,"235006b0-8f14-4ca2-82f0-f96b6b8c4766"),sQuery(id+"F3.wireOp",EDGE,"0fc7acd6-1c1d-47a8-ba12-62eb658d35ca"),sQuery(id+"F3.wireOp",EDGE,"883fa5e3-ca4c-4ce6-a249-4debf538fe24"),sQuery(id+"F3.wireOp",EDGE,"1da09ed1-22d9-43a1-a655-8acff5d61309"),sQuery(id+"F3.wireOp",EDGE,"32654a82-a09a-444f-bf73-45f818f0f235"),sQuery(id+"F3.wireOp",EDGE,"a398fd80-a0a9-4724-ba0e-1a7a000baa92"),sQuery(id+"F3.wireOp",EDGE,"f39f97c8-53f5-4046-9905-b28daecd4f10"),sQuery(id+"F3.wireOp",EDGE,"2484d883-0ec2-4c7d-9023-165ebbef226c"),sQuery(id+"F3.wireOp",EDGE,"f026d96f-3d32-4113-a1c9-3545f5cdbe4a"),sQuery(id+"F3.wireOp",EDGE,"974fee18-719e-4620-aace-d3676da2011b"),sQuery(id+"F3.wireOp",EDGE,"0c5766d2-a026-45af-bffd-0d1f783d5157"),sQuery(id+"F3.wireOp",EDGE,"5da13fee-9c04-45d8-805f-c7a03dde2383"),sQuery(id+"F3.wireOp",EDGE,"dbea32a3-85bd-4957-aef2-b6fe64a02f6b"),sQuery(id+"F3.wireOp",EDGE,"fba134ea-bf40-4191-ad8f-cc6b2b040a97"),sQuery(id+"F3.wireOp",EDGE,"0c19e200-7cd5-4fcb-83ed-261bd7936bc7"),sQuery(id+"F3.wireOp",EDGE,"246b843b-ea86-44e5-9cb9-335e6677b61d"),sQuery(id+"F3.wireOp",EDGE,"c1b3c9bc-1eb4-4c9b-99c8-0cebed89395a"),sQuery(id+"F3.wireOp",EDGE,"f93eebc3-1447-4029-8362-91325193ac2b"),sQuery(id+"F3.wireOp",EDGE,"bf86b12d-53a9-4c19-abaa-b1e658933ceb"),sQuery(id+"F3.wireOp",EDGE,"89646a71-1a60-4e14-b80a-74fb601d0855"),sQuery(id+"F3.wireOp",EDGE,"7b03dcde-0a52-4f3c-80e9-110d1d805e93"),sQuery(id+"F3.wireOp",EDGE,"83e8d1f3-8820-485b-8b6d-3ecd79124883"),sQuery(id+"F3.wireOp",EDGE,"ec7b56eb-ca95-44fd-a774-e9b7f9d3f50d"),sQuery(id+"F3.wireOp",EDGE,"31861aa6-cfd1-43ce-a7c5-bacfb7e2a30f"),sQuery(id+"F3.wireOp",EDGE,"fa3de647-1dd9-4141-982b-74ae8d07851d"),sQuery(id+"F3.wireOp",EDGE,"75d7c1c5-761c-4178-bfd4-4f469045899b"),sQuery(id+"F3.wireOp",EDGE,"4b3d7518-bd5d-4ecc-b2c5-d8dd665de4f4"),sQuery(id+"F3.wireOp",EDGE,"3be2682d-01bd-4f31-9cde-9df16a01e4a9"),sQuery(id+"F3.wireOp",EDGE,"72d3c7a9-2794-46eb-9b0d-6c526cc1b9a3"),sQuery(id+"F3.wireOp",EDGE,"0137e336-6b26-4f8d-b9ad-47ce1aa9eb31"),sQuery(id+"F3.wireOp",EDGE,"96000e4a-2d86-4b9f-af7d-a1c875cc048c"),sQuery(id+"F3.wireOp",EDGE,"139c5a79-9c0f-4e15-b57f-4c09662495a3"),sQuery(id+"F3.wireOp",EDGE,"8ea04d8b-b3da-46bb-9742-d8cba6b23bda"),sQuery(id+"F3.wireOp",EDGE,"b352b580-467e-481c-88ac-6217b8462947"),sQuery(id+"F3.wireOp",EDGE,"2503a493-1722-4539-8d54-7329fc0b116a"),sQuery(id+"F3.wireOp",EDGE,"a0615e06-0a48-4c65-8818-f0f693937022"),sQuery(id+"F3.wireOp",EDGE,"08389002-1ce8-438a-b5a4-698ca33590c2"),sQuery(id+"F3.wireOp",EDGE,"1756e4aa-c30a-461e-962c-81ee35d31e55"),sQuery(id+"F3.wireOp",EDGE,"5f84c249-07ea-4efb-9be3-ca494937f772"),sQuery(id+"F3.wireOp",EDGE,"cbefd041-b54f-4587-87b6-437b2290d1fc"),sQuery(id+"F3.wireOp",EDGE,"d44f58d4-f1a7-4aec-b016-8e7f1e498aeb"),sQuery(id+"F3.wireOp",EDGE,"0a5be90b-7545-44ea-9f2d-c726a5a2121c"),sQuery(id+"F3.wireOp",EDGE,"0cfaa442-d102-4580-8ef6-489f2aa1e6b3")])]});
            var Q2;
            Q2=makeQuery(id+"F4.opExtrude","SWEPT_BODY",BODY,{"disambiguationData":[OSD([sQuery(id+"F3.wireOp",EDGE,"9cc7aec6-4d94-4577-ab6c-32f5aa316238"),sQuery(id+"F3.wireOp",EDGE,"5ab2d840-4a32-405a-8c4b-a8126e3e1bc1"),sQuery(id+"F3.wireOp",EDGE,"56de48b4-9620-4637-8196-310e2641530f"),sQuery(id+"F3.wireOp",EDGE,"55327826-e64b-4830-85f2-3f22d36f43b5"),sQuery(id+"F3.wireOp",EDGE,"0245b46f-a639-4a95-8ca3-1568736ceed2"),sQuery(id+"F3.wireOp",EDGE,"9bd8a002-6ca7-4c84-8984-a620eefad103"),sQuery(id+"F3.wireOp",EDGE,"d4736c5e-da0b-46a0-ba9d-17ae07bb2b66"),sQuery(id+"F3.wireOp",EDGE,"125695b8-77e6-4e99-8f78-5f8fae1a0c71"),sQuery(id+"F3.wireOp",EDGE,"c9f25b10-a495-4684-8f25-8f255fabab6e"),sQuery(id+"F3.wireOp",EDGE,"0dbee67a-2ab6-4abb-ae16-0fe64d623848"),sQuery(id+"F3.wireOp",EDGE,"92c08d8e-ed2e-41a3-9c1a-b5ddaf8a0bf1"),sQuery(id+"F3.wireOp",EDGE,"00fabb15-0c1e-492e-85c1-17390e5b12bc"),sQuery(id+"F3.wireOp",EDGE,"065a9352-dddb-4e3f-b02a-444c867b75fe"),sQuery(id+"F3.wireOp",EDGE,"ef206bb6-e4f2-4189-9fc7-a7823c329ad6"),sQuery(id+"F3.wireOp",EDGE,"7199cbbe-c9bf-4cb9-b928-2ff8a84eb09e"),sQuery(id+"F3.wireOp",EDGE,"17bf9ed1-b881-4f74-816d-3511b6b328c7"),sQuery(id+"F3.wireOp",EDGE,"e5b615d0-4193-495d-b285-bd69ae30f000"),sQuery(id+"F3.wireOp",EDGE,"cfeaf62f-6be1-426b-9732-01e1a667be7e"),sQuery(id+"F3.wireOp",EDGE,"ac56344b-5ee6-4fa5-8e47-65b2a4ea3a01"),sQuery(id+"F3.wireOp",EDGE,"45b5fa53-15fd-43a0-91b0-943cc3286fc9")])]});
            var Q3;
            Q3=makeQuery(id+"F4.opExtrude","SWEPT_BODY",BODY,{"disambiguationData":[OSD([sQuery(id+"F3.wireOp",EDGE,"7bdfe37d-9957-4663-8239-5490fd3220d9"),sQuery(id+"F3.wireOp",EDGE,"6a91314f-c002-4565-bbf8-bb9f29165fb8"),sQuery(id+"F3.wireOp",EDGE,"b69f99c7-a6d0-4d1b-8752-9e82ab4c99ec"),sQuery(id+"F3.wireOp",EDGE,"c928f899-12af-4b01-b412-b3b7da3d830f"),sQuery(id+"F3.wireOp",EDGE,"ffa58721-cdd5-406d-be26-d96f7a050df4"),sQuery(id+"F3.wireOp",EDGE,"02fc7fb8-293b-44ff-ab78-63506d0aedb9"),sQuery(id+"F3.wireOp",EDGE,"147fb6cb-2565-4fb5-9280-6afbf9eef36b"),sQuery(id+"F3.wireOp",EDGE,"2cee3704-4124-415a-b391-31af1cf305d7"),sQuery(id+"F3.wireOp",EDGE,"32b2fb71-03c8-4978-9d95-2b5aaf044d0d"),sQuery(id+"F3.wireOp",EDGE,"e5d05796-7d6c-4350-8a4e-d55f5ade2f77"),sQuery(id+"F3.wireOp",EDGE,"77b1164c-8dd4-4680-b616-ac151a422eb2"),sQuery(id+"F3.wireOp",EDGE,"ec0798b8-0fbb-49ea-9766-39d2ee0936b0"),sQuery(id+"F3.wireOp",EDGE,"c4af6478-2a03-47a6-862f-c0c71886b8a3"),sQuery(id+"F3.wireOp",EDGE,"1912a38f-fa28-45c6-ab33-84cac2787056"),sQuery(id+"F3.wireOp",EDGE,"5d79fa95-f66d-4d2b-923b-4d54735f1fbd"),sQuery(id+"F3.wireOp",EDGE,"2db7aef4-a710-4bcf-9c1c-a8a87719953d"),sQuery(id+"F3.wireOp",EDGE,"183449de-345c-4115-9bca-43a403e62dbd"),sQuery(id+"F3.wireOp",EDGE,"e3ac8c9b-cab5-44b0-ad81-0e2b680c384a"),sQuery(id+"F3.wireOp",EDGE,"92e85db6-f458-41f6-a9a1-1e1a1a7e7809"),sQuery(id+"F3.wireOp",EDGE,"f0dbb46f-43a9-447b-9c75-8dfc9b95470d"),sQuery(id+"F3.wireOp",EDGE,"4b73f5f6-f769-4414-bdba-7d253e58fff4"),sQuery(id+"F3.wireOp",EDGE,"a88669dc-35b3-46bb-964f-c9bf6c4ab898"),sQuery(id+"F3.wireOp",EDGE,"2c559bae-f38f-4377-91e6-3c9de70acf11"),sQuery(id+"F3.wireOp",EDGE,"c1caf99b-adaa-42fe-a319-8cbcd819cf89"),sQuery(id+"F3.wireOp",EDGE,"54b04dd4-0ec4-4956-b19c-1141095738e3"),sQuery(id+"F3.wireOp",EDGE,"098f7a84-b7b8-4879-b21a-5c38879e4110"),sQuery(id+"F3.wireOp",EDGE,"b406a8e6-a226-4f3d-ac30-e4d06e4dac62"),sQuery(id+"F3.wireOp",EDGE,"36f95d1d-68ce-4231-ad71-3960c85e5915"),sQuery(id+"F3.wireOp",EDGE,"dc12cad8-2eed-454e-aa74-30099b1c9064"),sQuery(id+"F3.wireOp",EDGE,"4c78a4fd-cd81-43d6-85d6-6e4d3fbc1e98"),sQuery(id+"F3.wireOp",EDGE,"ee9e30de-787b-4e8f-b425-43a8e9289f81"),sQuery(id+"F3.wireOp",EDGE,"2518a3a4-c96b-4463-8704-0b71c65c60d2"),sQuery(id+"F3.wireOp",EDGE,"c9129a67-398c-4e37-92cb-2d54ff2e2e82"),sQuery(id+"F3.wireOp",EDGE,"d429d547-9f5b-42c6-bcca-effad2fa908f"),sQuery(id+"F3.wireOp",EDGE,"99d16e94-b2b3-43d5-9c7b-7bd463994dcb"),sQuery(id+"F3.wireOp",EDGE,"32993909-9a70-47ee-9097-89fff220f839"),sQuery(id+"F3.wireOp",EDGE,"6eabbeed-9496-4825-b168-63782a34f495"),sQuery(id+"F3.wireOp",EDGE,"f74987e3-8e60-4a5b-857f-839ae8aaf0cf"),sQuery(id+"F3.wireOp",EDGE,"1c218c86-035d-4441-93c0-9621d3297c3a"),sQuery(id+"F3.wireOp",EDGE,"0133f513-4b11-4cc4-b075-4625e9591e41"),sQuery(id+"F3.wireOp",EDGE,"fe921ad4-a8f5-4772-9aeb-350aca2e8948"),sQuery(id+"F3.wireOp",EDGE,"bfde0a4f-3cec-4f8e-8a23-dd1441b34c2b"),sQuery(id+"F3.wireOp",EDGE,"b41521ff-c5df-4b64-83ed-5e7635cf4438"),sQuery(id+"F3.wireOp",EDGE,"ed692599-6bbb-4379-8e89-ea326a0a0f87"),sQuery(id+"F3.wireOp",EDGE,"a98451c0-d76c-436e-99f9-a3fe9c8430a4"),sQuery(id+"F3.wireOp",EDGE,"561965b2-3050-4f49-9305-d98a2b852bbe"),sQuery(id+"F3.wireOp",EDGE,"e13dfa59-48e6-4b4e-94b9-1fc5254b0f2e"),sQuery(id+"F3.wireOp",EDGE,"0354e106-253a-4bfa-b5b7-b09cd0f2f6c0"),sQuery(id+"F3.wireOp",EDGE,"8df1dcc8-d00a-4777-85fd-8af8e9830bd1"),sQuery(id+"F3.wireOp",EDGE,"26ce3762-0d1a-4b81-9a23-debcfc24da1c"),sQuery(id+"F3.wireOp",EDGE,"3e900f8f-3ffb-4e32-b536-61fea2f3e30a"),sQuery(id+"F3.wireOp",EDGE,"4a1b5445-5559-461f-b6f1-b4cd9b95ea10")])]});
            var Q4;
            Q4=makeQuery(id+"F1.opRevolve","SWEPT_BODY",BODY,{"disambiguationData":[OSD([sQuery(id+"F0.wireOp",EDGE,"E0"),sQuery(id+"F0.wireOp",EDGE,"E1")])]});
            var Q5;
            Q5=qCreatedBy(makeId("Origin.pointOp"),VERTEX);
            transform(context, id + "F5", {"entities" : qUnion([Q0, Q1, Q2, Q3, Q4]), "transformType" : TransformType.SCALE_UNIFORMLY, "scale" : 0.03, "scalePoint" : qUnion([Q5]), "makeCopy" : false});
        }
        {
            var Q0;
            Q0=qCreatedBy(makeId("Top.planeOp"),FACE);
            var sketch = newSketch(context, id + "F6", { "sketchPlane" : qUnion([Q0])});
            skLineSegment(sketch, "E180", {"start": v(0, 15) * mm, "end": v(0, -15) * mm});
            skArc(sketch, "E181", {"start": v(0, 15) * mm, "mid": v(-15, 0) * mm, "end": v(0, -15) * mm});
            skArc(sketch, "E182", {"start": v(0, 10.25) * mm, "mid": v(-10.25, 0) * mm, "end": v(0, -10.25) * mm});
            skArc(sketch, "E183", {"start": v(0, 7) * mm, "mid": v(-7, 0) * mm, "end": v(0, -7) * mm});
            skSolve(sketch);
        }
        {
            var Q0;
            {var subQ0=sQuery(id+"F6.wireOp",EDGE,"E181");Q0=makeQuery(id+"F6.imprint","IMPRINT",FACE,{"disambiguationData":[TD([[makeQuery(id+"F6.imprint","IMPRINT",EDGE,{"derivedFrom":subQ0}),1.0]])]});}
            var Q1;
            {var subQ0=sQuery(id+"F6.wireOp",EDGE,"E183");Q1=makeQuery(id+"F6.imprint","IMPRINT",FACE,{"disambiguationData":[TD([[makeQuery(id+"F6.imprint","IMPRINT",EDGE,{"derivedFrom":subQ0}),1.0]])]});}
            var Q2;
            Q2=sQuery(id+"F6.wireOp",EDGE,"E180");
            revolve(context, id + "F7", {"operationType" : NewBodyOperationType.REMOVE, "entities" : qUnion([Q0, Q1]), "axis" : qUnion([Q2]), "revolveType" : RevolveType.FULL});
        }
        {
            var Q0;
            Q0=makeQuery(id+"F1.opRevolve","SWEPT_BODY",BODY,{"disambiguationData":[OSD([sQuery(id+"F0.wireOp",EDGE,"E0"),sQuery(id+"F0.wireOp",EDGE,"E1")])]});
            var Q1;
            Q1=sQuery(id+"F0.wireOp",VERTEX,"E1.center");
            transform(context, id + "F8", {"entities" : qUnion([Q0]), "transformType" : TransformType.SCALE_UNIFORMLY, "scale" : 1.4, "scalePoint" : qUnion([Q1]), "makeCopy" : false});
        }
        {
            var Q0;
            Q0=qCreatedBy(makeId("Front.planeOp"),FACE);
            var sketch = newSketch(context, id + "F9", { "sketchPlane" : qUnion([Q0])});
            skCircle(sketch, "E184", {"center": v(0, -5.12) * mm, "radius": 2 * mm});
            skSolve(sketch);
        }
        {
            var Q0;
            Q0=qSketchRegion(id+"F9",true);
            extrude(context, id + "F10", {"entities" : qUnion([Q0]), "operationType" : NewBodyOperationType.REMOVE, "oppositeDirection" : true, "depth" : 25 * mm});
        }
        {
            var Q0;
            Q0=qCreatedBy(makeId("Top.planeOp"),FACE);
            var sketch = newSketch(context, id + "F11", { "sketchPlane" : qUnion([Q0])});
            skLineSegment(sketch, "E185", {"start": v(-27.1, 0) * mm, "end": v(32.5, 0) * mm});
            skArc(sketch, "E186", {"start": v(-14.25, 0) * mm, "mid": v(0, 14.25) * mm, "end": v(14.25, 0) * mm});
            skSolve(sketch);
        }
        {
            var Q0;
            Q0=sQuery(id+"F11.wireOp",EDGE,"E185");
            cPlane(context, id + "F12", {"entities" : qUnion([Q0]), "cplaneType" : CPlaneType.LINE_ANGLE, "offset" : 25 * mm, "angle" : 40 * degree, "width" : 150 * mm, "height" : 150 * mm});
        }
        {
            var Q0;
            Q0=qCreatedBy(id+"F12.planeOp",FACE);
            var sketch = newSketch(context, id + "F13", { "sketchPlane" : qUnion([Q0])});
            skText(sketch, "E187", { "text": "insight", "fontName": "OpenSans-Italic.ttf"});
            const initialGuessF13  = {"E187": [-0.00837, -0.003, 1, 0, 0.004]};
            skSetInitialGuess(sketch, initialGuessF13);
            skSolve(sketch);
        }
        {
            var Q0;
            Q0=sQuery(id+"F11.wireOp",EDGE,"E186");
            var Q1;
            Q1=sQuery(id+"F11.wireOp",EDGE,"E185");
            revolve(context, id + "F14", {"bodyType" : ToolBodyType.SURFACE, "surfaceEntities" : qUnion([Q0]), "axis" : qUnion([Q1]), "revolveType" : RevolveType.FULL});
        }
        {
            var Q0;
            Q0 = qSketchRegion(id + "F13", true);
            var Q1;
            Q1=makeQuery(id+"F14.opRevolve","SWEPT_FACE",FACE,{"disambiguationData":[OSD([sQuery(id+"F11.wireOp",EDGE,"E186")])]});
            extrude(context, id + "F15", {"entities" : qUnion([Q0]), "operationType" : NewBodyOperationType.ADD, "endBound" : BoundingType.UP_TO_SURFACE, "depth" : 25 * mm, "endBoundEntityFace" : qUnion([Q1]), "offsetDistance" : 25 * mm});
        }
    });
